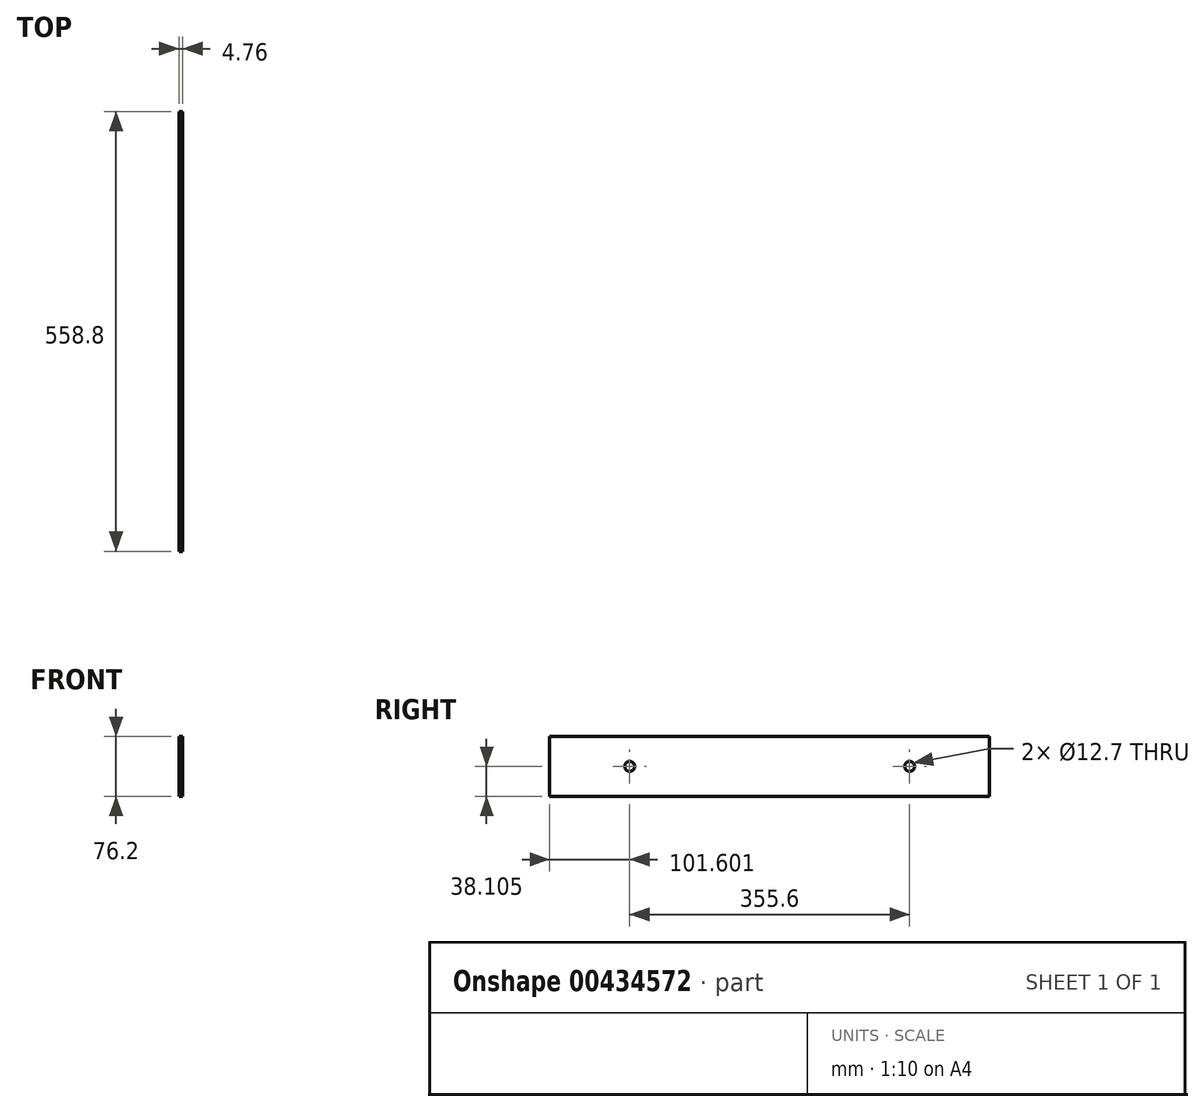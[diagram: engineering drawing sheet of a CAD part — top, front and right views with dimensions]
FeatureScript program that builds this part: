
annotation { "Feature Type Name" : "Feature", "Feature Type Description" : "" }
export const myFeature = defineFeature(function(context is Context, id is Id, definition is map)
    precondition{}
    {
        {
            var Q0;
            Q0=qCreatedBy(makeId("Right.planeOp"),FACE);
            var sketch = newSketch(context, id + "F0", { "sketchPlane" : qUnion([Q0])});
            skLineSegment(sketch, "E0.bottom", {"start": v(-81.74, 63.68) * mm, "end": v(477.06, 63.68) * mm});
            skLineSegment(sketch, "E0.top", {"start": v(-81.74, -12.52) * mm, "end": v(477.06, -12.52) * mm});
            skLineSegment(sketch, "E0.left", {"start": v(-81.74, 63.68) * mm, "end": v(-81.74, -12.52) * mm});
            skLineSegment(sketch, "E0.right", {"start": v(477.06, 63.68) * mm, "end": v(477.06, -12.52) * mm});
            skCircle(sketch, "E1", {"center": v(19.86, 25.58) * mm, "radius": 6.35 * mm});
            skCircle(sketch, "E2", {"center": v(375.46, 25.58) * mm, "radius": 6.35 * mm});
            skSolve(sketch);
        }
        {
            var Q0;
            Q0=makeQuery(id+"F0.imprint","IMPRINT",FACE,{"disambiguationData":[TD([[makeQuery(id+"F0.imprint","IMPRINT",EDGE,{"derivedFrom":sQuery(id+"F0.wireOp",EDGE,"E0.bottom")}),-1.0]])]});
            extrude(context, id + "F1", {"entities" : qUnion([Q0]), "depth" : 4.76 * mm});
        }
    });
